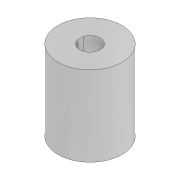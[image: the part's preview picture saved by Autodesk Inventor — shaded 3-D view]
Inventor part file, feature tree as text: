
AUTODESK INVENTOR PART (.ipt)
format: ipt  version: 2022 (Build 260153000, 153)  size: 96,256 bytes
history: native  units: mm
features: extrude x2, sketch x2
ambient origin geometry x8: Origin, YZ Plane, XZ Plane, XY Plane, X Axis, Y Axis, Z Axis, Center Point
bodies: Solid1 (feature_tree)
feature tree (4):
  extrude  "Extrusion1"  Depth=25.0mm TaperAngle=0.0deg
  extrude  "Extrusion2"  Depth=6.0mm
  sketch  "Sketch1"  dims[d0=20.0mm d1=25.0mm d2=0.0mm]
  sketch  "Sketch2"  dims[d3=6.4mm d4=6.1mm d5=6.0mm d6=0.0mm]
